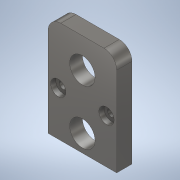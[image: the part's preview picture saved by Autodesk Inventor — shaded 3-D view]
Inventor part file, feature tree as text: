
AUTODESK INVENTOR PART (.ipt)
format: ipt  version: 2020 (Build 240168000, 168)  size: 183,296 bytes
history: native  units: mm
features: sketch x4, projected_geometry x4, extrude x2, hole x2, fillet x1
ambient origin geometry x8: Origin, YZ Plane, XZ Plane, XY Plane, X Axis, Y Axis, Z Axis, Center Point
bodies: Volumenkörper1 (feature_tree)
feature tree (13):
  extrude  "Extrusion1"  Depth=10.0mm
  hole  "Bohrung1"  [1 undecoded]
  extrude  "Extrusion2"  Depth=6.0mm TaperAngle=0.0deg
  fillet  "Fillet2"  Radius=4.0mm
  hole  "Hole5"  [1 undecoded]
  sketch  "Skizze1"  dims[d0=27.0mm d1=10.0mm]
  sketch  "Skizze2"  dims[d2=10.0mm d3=21.5mm]
  projected_geometry  "Projizierte Kontur1"
  sketch  "Skizze5"  dims[d4=21.5mm d5=6.0mm d6=0.0mm d8=4.0mm]
  projected_geometry  "Projizierte Kontur3"
  projected_geometry  "Projizierte Kontur4"
  sketch  "Sketch7"  dims[d10=2.459mm d11=6.0mm d12=4.0mm d13=2.0mm d14=90.0deg d15=8.0mm d16=20.594885mm d35=40.0mm d44=21.1mm d45=1.0mm d46=0.0mm d55=5.0mm d58=3.2mm d59=6.0mm d60=6.0mm d61=2.0mm d62=90.0deg d63=8.0mm d64=20.594885mm d66=9.5mm d67=9.5mm d68=9.5mm d65=1.0mm d69=0.25mm d70=0.375mm d71=14.3117mm d72=0.75mm d73=20.594885mm d74=0.0625mm d75=0.75mm d76=0.375mm]
  projected_geometry  "Projected Loop5"
note: 2 required parameter values undecoded (feature->parameter linkage not recoverable at this tier; creation-order binding heuristic only, values carry confidence <= 0.55)
